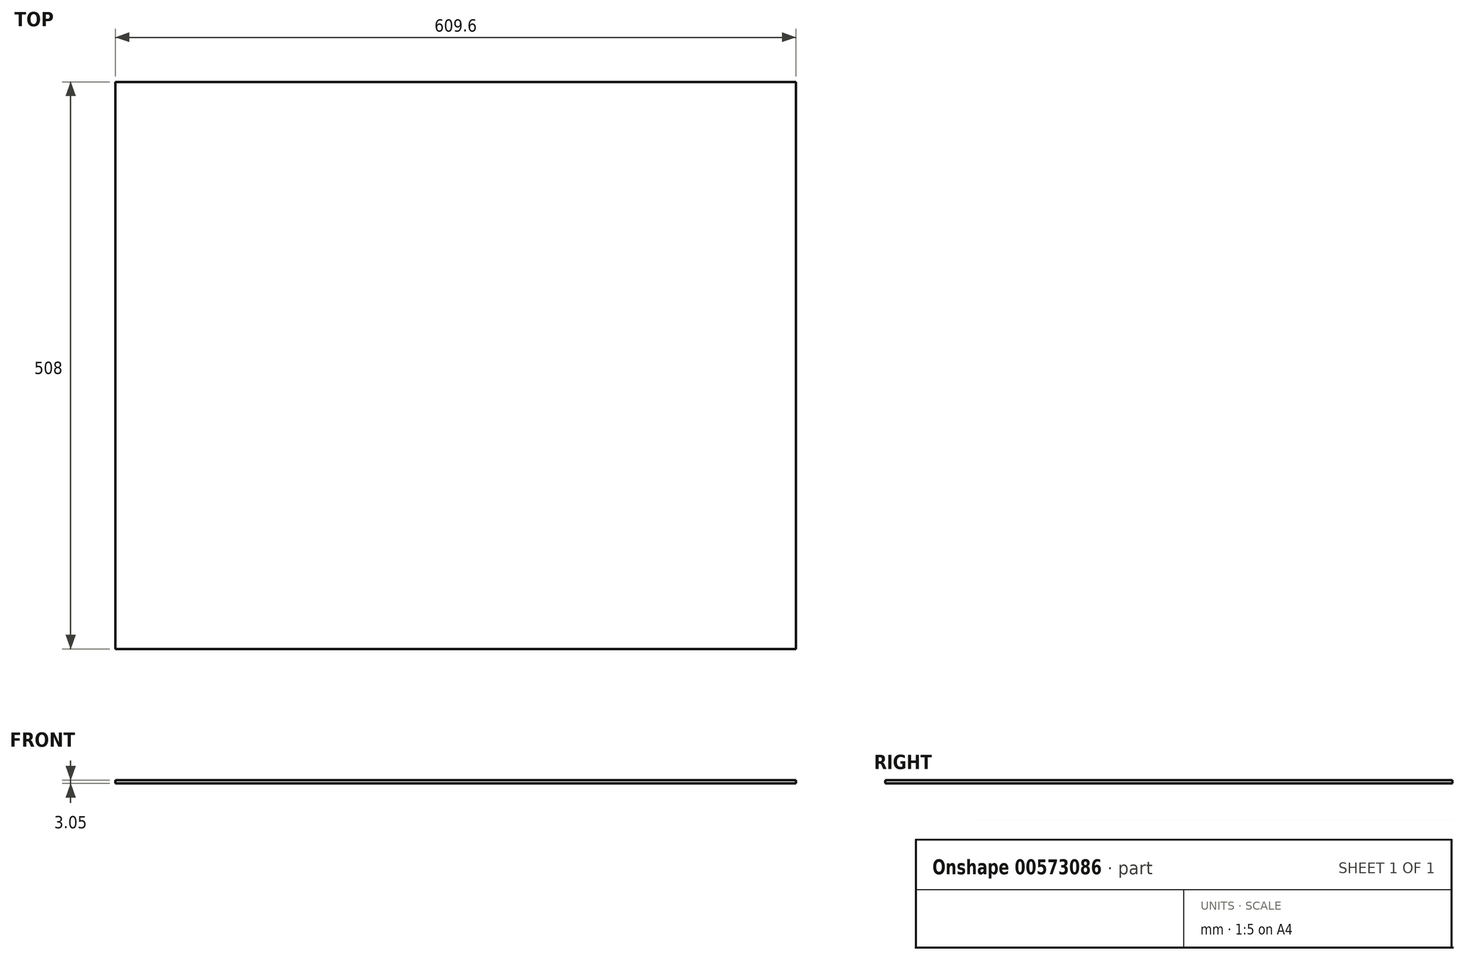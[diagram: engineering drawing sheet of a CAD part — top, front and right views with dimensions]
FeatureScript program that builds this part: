
annotation { "Feature Type Name" : "Feature", "Feature Type Description" : "" }
export const myFeature = defineFeature(function(context is Context, id is Id, definition is map)
    precondition{}
    {
        {
            var Q0;
            Q0=qCreatedBy(makeId("Top.planeOp"),FACE);
            var sketch = newSketch(context, id + "F0", { "sketchPlane" : qUnion([Q0])});
            skLineSegment(sketch, "E0.bottom", {"start": v(304.8, 254) * mm, "end": v(-304.8, 254) * mm});
            skLineSegment(sketch, "E0.top", {"start": v(304.8, -254) * mm, "end": v(-304.8, -254) * mm});
            skLineSegment(sketch, "E0.left", {"start": v(304.8, 254) * mm, "end": v(304.8, -254) * mm});
            skLineSegment(sketch, "E0.right", {"start": v(-304.8, 254) * mm, "end": v(-304.8, -254) * mm});
            skPoint(sketch, "E0.middle", {"position": v(0, 0) * mm});
            skSolve(sketch);
        }
        {
            var Q0;
            Q0=makeQuery(id+"F0.imprint","IMPRINT",FACE,{"disambiguationData":[TD([[makeQuery(id+"F0.imprint","IMPRINT",EDGE,{"derivedFrom":sQuery(id+"F0.wireOp",EDGE,"E0.bottom")}),1.0]])]});
            extrude(context, id + "F1", {"entities" : qUnion([Q0]), "depth" : 3.05 * mm, "offsetDistance" : 25.4 * mm});
        }
    });
